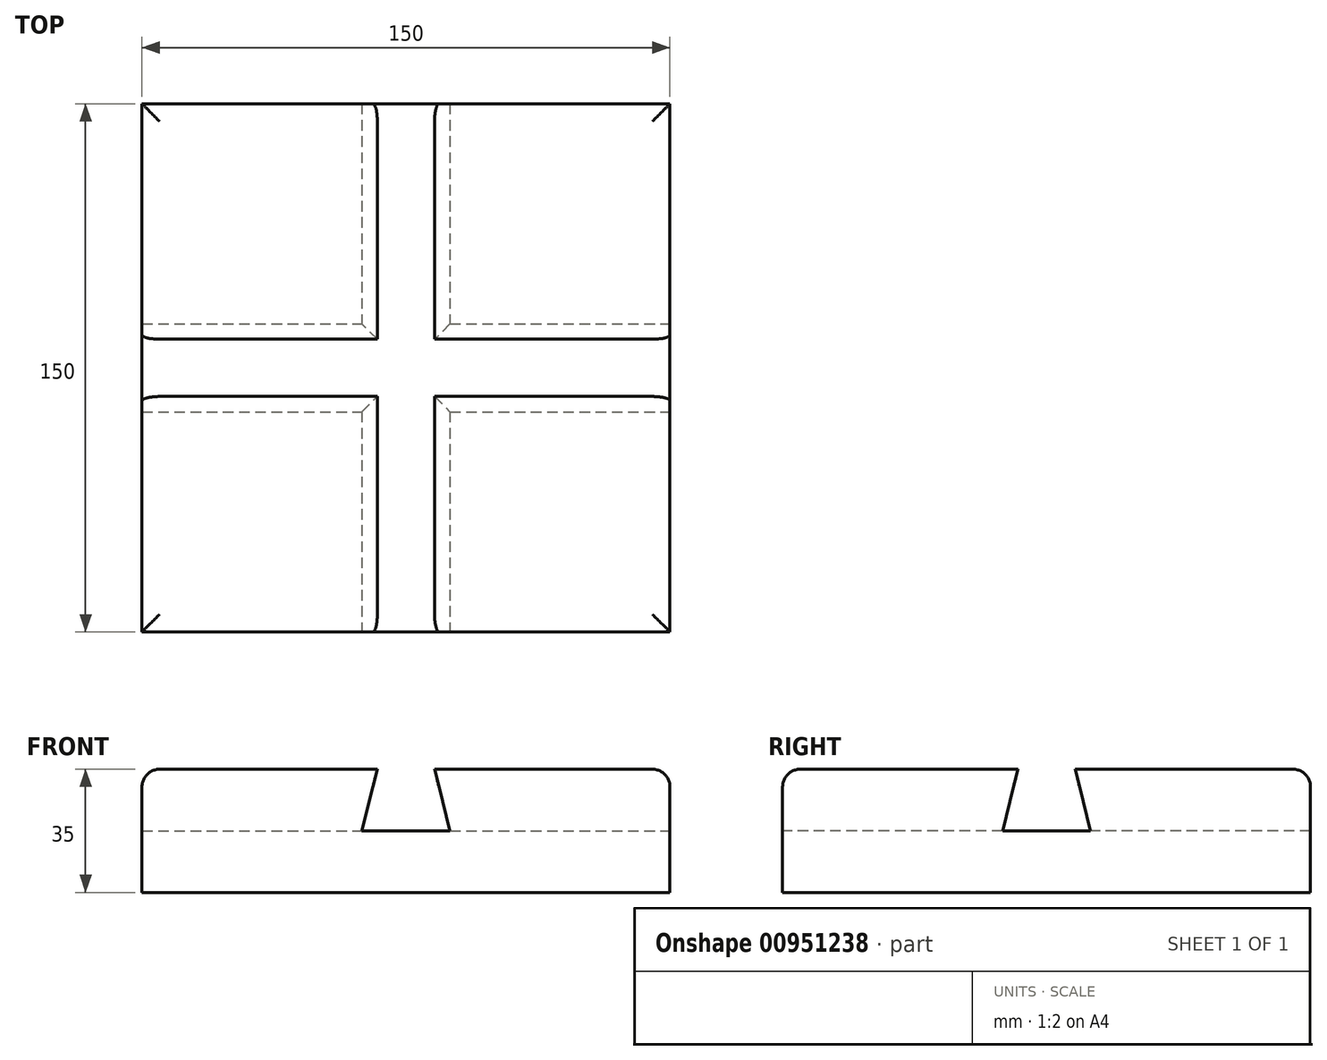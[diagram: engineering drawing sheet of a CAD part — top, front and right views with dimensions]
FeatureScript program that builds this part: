
annotation { "Feature Type Name" : "Feature", "Feature Type Description" : "" }
export const myFeature = defineFeature(function(context is Context, id is Id, definition is map)
    precondition{}
    {
        {
            var Q0;
            Q0=qCreatedBy(makeId("Top.planeOp"),FACE);
            var sketch = newSketch(context, id + "F0", { "sketchPlane" : qUnion([Q0])});
            skLineSegment(sketch, "E0.bottom", {"start": v(75, -75) * mm, "end": v(-75, -75) * mm});
            skLineSegment(sketch, "E0.top", {"start": v(75, 75) * mm, "end": v(-75, 75) * mm});
            skLineSegment(sketch, "E0.left", {"start": v(75, -75) * mm, "end": v(75, 75) * mm});
            skLineSegment(sketch, "E0.right", {"start": v(-75, -75) * mm, "end": v(-75, 75) * mm});
            skPoint(sketch, "E0.middle", {"position": v(0, 0) * mm});
            skSolve(sketch);
        }
        {
            var Q0;
            Q0=makeQuery(id+"F0.imprint","IMPRINT",FACE,{"disambiguationData":[TD([[makeQuery(id+"F0.imprint","IMPRINT",EDGE,{"derivedFrom":sQuery(id+"F0.wireOp",EDGE,"E0.bottom")}),-1.0]])]});
            extrude(context, id + "F1", {"entities" : qUnion([Q0]), "depth" : 35 * mm, "offsetDistance" : 25 * mm, "symmetric" : true});
        }
        {
            var Q0;
            Q0=makeQuery(id+"F1.opExtrude","SWEPT_FACE",FACE,{"disambiguationData":[OSD([sQuery(id+"F0.wireOp",EDGE,"E0.bottom")])]});
            var sketch = newSketch(context, id + "F2", { "sketchPlane" : qUnion([Q0])});
            skLineSegment(sketch, "E1", {"start": v(-12.5, 0) * mm, "end": v(12.5, 0) * mm});
            skLineSegment(sketch, "E2", {"start": v(12.5, 0) * mm, "end": v(8.14, 17.5) * mm});
            skLineSegment(sketch, "E3", {"start": v(8.14, 17.5) * mm, "end": v(-8.14, 17.5) * mm});
            skLineSegment(sketch, "E4", {"start": v(-8.14, 17.5) * mm, "end": v(-12.5, 0) * mm});
            skPoint(sketch, "E5", {"position": v(0, 0) * mm});
            skSolve(sketch);
        }
        {
            var Q0;
            Q0=makeQuery(id+"F2.imprint","IMPRINT",FACE,{"disambiguationData":[TD([[makeQuery(id+"F2.imprint","IMPRINT",EDGE,{"derivedFrom":sQuery(id+"F2.wireOp",EDGE,"E1")}),1.0]])]});
            extrude(context, id + "F3", {"entities" : qUnion([Q0]), "operationType" : NewBodyOperationType.REMOVE, "endBound" : BoundingType.THROUGH_ALL, "oppositeDirection" : true, "depth" : 25 * mm, "offsetDistance" : 25 * mm});
        }
        {
            var Q0;
            Q0=makeQuery(id+"F1.opExtrude","SWEPT_FACE",FACE,{"disambiguationData":[OSD([sQuery(id+"F0.wireOp",EDGE,"E0.left")])]});
            var sketch = newSketch(context, id + "F4", { "sketchPlane" : qUnion([Q0])});
            skLineSegment(sketch, "E6", {"start": v(-12.5, 0) * mm, "end": v(12.5, 0) * mm});
            skLineSegment(sketch, "E7", {"start": v(12.5, 0) * mm, "end": v(8.14, 17.5) * mm});
            skLineSegment(sketch, "E8", {"start": v(8.14, 17.5) * mm, "end": v(-8.14, 17.5) * mm});
            skLineSegment(sketch, "E9", {"start": v(-8.14, 17.5) * mm, "end": v(-12.5, 0) * mm});
            skPoint(sketch, "E10", {"position": v(0, 0) * mm});
            skSolve(sketch);
        }
        {
            var Q0;
            Q0=makeQuery(id+"F4.imprint","IMPRINT",FACE,{"disambiguationData":[TD([[makeQuery(id+"F4.imprint","IMPRINT",EDGE,{"derivedFrom":sQuery(id+"F4.wireOp",EDGE,"E6")}),1.0]])]});
            extrude(context, id + "F5", {"entities" : qUnion([Q0]), "operationType" : NewBodyOperationType.REMOVE, "endBound" : BoundingType.THROUGH_ALL, "oppositeDirection" : true, "depth" : 227.8 * mm, "offsetDistance" : 25 * mm});
        }
        {
            var Q0;
            {var subQ0=sQuery(id+"F0.wireOp",EDGE,"E0.bottom");var subQ1=sQuery(id+"F0.wireOp",EDGE,"E0.right");Q0=makeQuery(id+"F5.boolean.opBoolean","SPLIT",EDGE,{"disambiguationData":[TD([makeQuery(id+"F1.opExtrude","SWEPT_FACE",FACE,{"disambiguationData":[OSD([subQ0])]})])],"derivedFrom":makeQuery(id+"F1.opExtrude","CAP_EDGE",EDGE,{"disambiguationData":[OSD([subQ1])],"isStart":false})});}
            var Q1;
            {var subQ0=sQuery(id+"F0.wireOp",EDGE,"E0.bottom");var subQ1=sQuery(id+"F0.wireOp",EDGE,"E0.right");Q1=makeQuery(id+"F3.boolean.opBoolean","SPLIT",EDGE,{"disambiguationData":[TD([makeQuery(id+"F1.opExtrude","SWEPT_FACE",FACE,{"disambiguationData":[OSD([subQ1])]})])],"derivedFrom":makeQuery(id+"F1.opExtrude","CAP_EDGE",EDGE,{"disambiguationData":[OSD([subQ0])],"isStart":false})});}
            var Q2;
            {var subQ0=sQuery(id+"F0.wireOp",EDGE,"E0.bottom");var subQ1=sQuery(id+"F0.wireOp",EDGE,"E0.left");Q2=makeQuery(id+"F3.boolean.opBoolean","SPLIT",EDGE,{"disambiguationData":[TD([makeQuery(id+"F1.opExtrude","SWEPT_FACE",FACE,{"disambiguationData":[OSD([subQ1])]})])],"derivedFrom":makeQuery(id+"F1.opExtrude","CAP_EDGE",EDGE,{"disambiguationData":[OSD([subQ0])],"isStart":false})});}
            var Q3;
            {var subQ0=sQuery(id+"F0.wireOp",EDGE,"E0.bottom");var subQ1=sQuery(id+"F0.wireOp",EDGE,"E0.left");Q3=makeQuery(id+"F5.boolean.opBoolean","SPLIT",EDGE,{"disambiguationData":[TD([makeQuery(id+"F1.opExtrude","SWEPT_FACE",FACE,{"disambiguationData":[OSD([subQ0])]})])],"derivedFrom":makeQuery(id+"F1.opExtrude","CAP_EDGE",EDGE,{"disambiguationData":[OSD([subQ1])],"isStart":false})});}
            var Q4;
            {var subQ0=sQuery(id+"F0.wireOp",EDGE,"E0.left");var subQ1=sQuery(id+"F0.wireOp",EDGE,"E0.top");Q4=makeQuery(id+"F5.boolean.opBoolean","SPLIT",EDGE,{"disambiguationData":[TD([makeQuery(id+"F1.opExtrude","SWEPT_FACE",FACE,{"disambiguationData":[OSD([subQ1])]})])],"derivedFrom":makeQuery(id+"F1.opExtrude","CAP_EDGE",EDGE,{"disambiguationData":[OSD([subQ0])],"isStart":false})});}
            var Q5;
            {var subQ0=sQuery(id+"F0.wireOp",EDGE,"E0.left");var subQ1=sQuery(id+"F0.wireOp",EDGE,"E0.top");Q5=makeQuery(id+"F3.boolean.opBoolean","SPLIT",EDGE,{"disambiguationData":[TD([makeQuery(id+"F1.opExtrude","SWEPT_FACE",FACE,{"disambiguationData":[OSD([subQ0])]})])],"derivedFrom":makeQuery(id+"F1.opExtrude","CAP_EDGE",EDGE,{"disambiguationData":[OSD([subQ1])],"isStart":false})});}
            var Q6;
            {var subQ0=sQuery(id+"F0.wireOp",EDGE,"E0.right");var subQ1=sQuery(id+"F0.wireOp",EDGE,"E0.top");Q6=makeQuery(id+"F3.boolean.opBoolean","SPLIT",EDGE,{"disambiguationData":[TD([makeQuery(id+"F1.opExtrude","SWEPT_FACE",FACE,{"disambiguationData":[OSD([subQ0])]})])],"derivedFrom":makeQuery(id+"F1.opExtrude","CAP_EDGE",EDGE,{"disambiguationData":[OSD([subQ1])],"isStart":false})});}
            var Q7;
            {var subQ0=sQuery(id+"F0.wireOp",EDGE,"E0.right");var subQ1=sQuery(id+"F0.wireOp",EDGE,"E0.top");Q7=makeQuery(id+"F5.boolean.opBoolean","SPLIT",EDGE,{"disambiguationData":[TD([makeQuery(id+"F1.opExtrude","SWEPT_FACE",FACE,{"disambiguationData":[OSD([subQ1])]})])],"derivedFrom":makeQuery(id+"F1.opExtrude","CAP_EDGE",EDGE,{"disambiguationData":[OSD([subQ0])],"isStart":false})});}
            fillet(context, id + "F6", {"entities" : qUnion([Q0, Q1, Q2, Q3, Q4, Q5, Q6, Q7]), "radius" : 5 * mm, "tangentPropagation" : true, "allowEdgeOverflow" : false});
        }
    });
